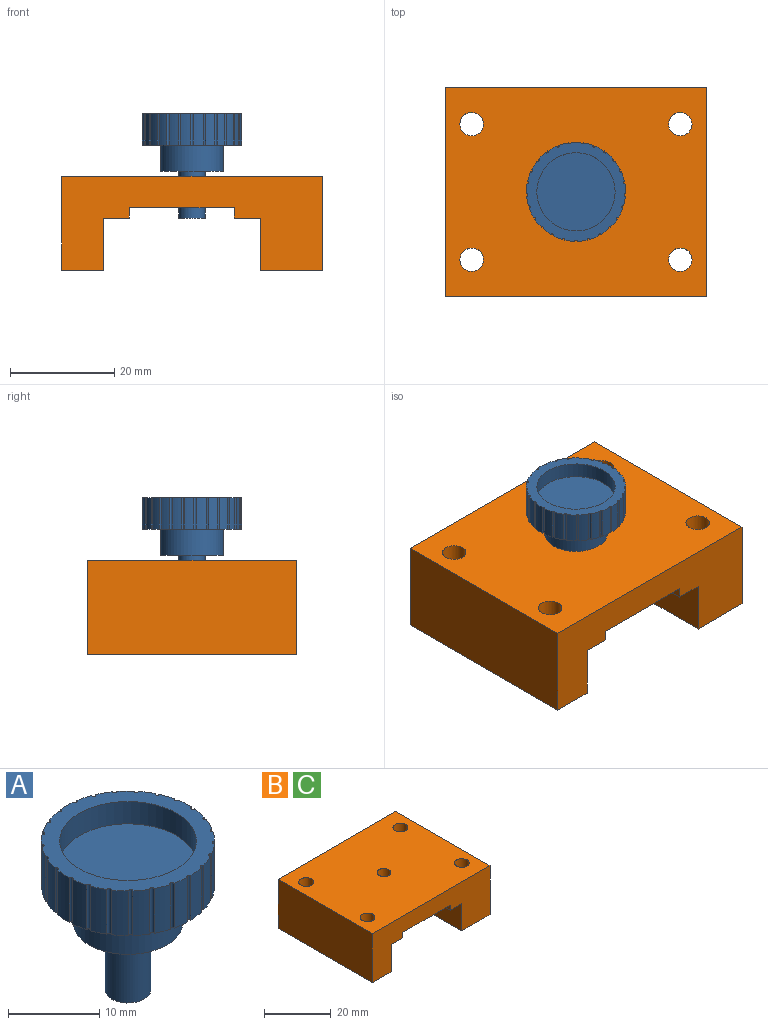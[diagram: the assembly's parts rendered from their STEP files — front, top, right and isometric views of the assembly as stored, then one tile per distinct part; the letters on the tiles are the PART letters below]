
ASSEMBLY  parts=3 mates=1
PART A: 58 faces, bbox 19x19x20 mm
  f0: plane 12x12mm, normal (0,0,-1), area 93.5mm2, adj f1,f3
  f1: cylinder r=2.5mm len=9mm, axis (0,0,1), area 141.4mm2, adj f0,f2
  f2: plane 5x5mm, normal (0,0,-1), area 19.6mm2, adj f1
  f3: cylinder r=6mm len=12mm, axis (0,0,-1), area 188.5mm2, adj f0,f4
  f4: plane 19x19mm, normal (0,0,-1), area 168mm2, adj f3,f6,f7,f8,f9,f10,f11,f12
  f5: plane 19x19mm, normal (0,0,1), area 104.4mm2, adj f6,f7,f8,f9,f10,f11,f12,f13
  f6: cylinder r=9.5mm len=6mm, axis (0,0,-1), area 11.3mm2, adj f4,f5,f7,f55
  f7: cylinder r=0.25mm len=6mm, axis (0,0,-1), area 4.7mm2, adj f4,f5,f6,f8
  f8: cylinder r=9.5mm len=6mm, axis (0,0,-1), area 11.3mm2, adj f4,f5,f7,f9
  f9: cylinder r=0.25mm len=6mm, axis (0,0,-1), area 4.7mm2, adj f4,f5,f8,f10
  f10: cylinder r=9.5mm len=6mm, axis (0,0,-1), area 11.3mm2, adj f4,f5,f9,f11
  f11: cylinder r=0.25mm len=6mm, axis (0,0,-1), area 4.7mm2, adj f4,f5,f10,f12
  f12: cylinder r=9.5mm len=6mm, axis (0,0,-1), area 11.3mm2, adj f4,f5,f11,f13
  f13: cylinder r=0.25mm len=6mm, axis (0,0,-1), area 4.7mm2, adj f4,f5,f12,f14
  f14: cylinder r=9.5mm len=6mm, axis (0,0,-1), area 11.3mm2, adj f4,f5,f13,f15
  f15: cylinder r=0.25mm len=6mm, axis (0,0,-1), area 4.7mm2, adj f4,f5,f14,f16
  f16: cylinder r=9.5mm len=6mm, axis (0,0,-1), area 11.3mm2, adj f4,f5,f15,f17
  f17: cylinder r=0.25mm len=6mm, axis (0,0,-1), area 4.7mm2, adj f4,f5,f16,f18
  f18: cylinder r=9.5mm len=6mm, axis (0,0,-1), area 11.3mm2, adj f4,f5,f17,f19
  f19: cylinder r=0.25mm len=6mm, axis (0,0,-1), area 4.7mm2, adj f4,f5,f18,f20
  f20: cylinder r=9.5mm len=6mm, axis (0,0,-1), area 11.3mm2, adj f4,f5,f19,f21
  f21: cylinder r=0.25mm len=6mm, axis (0,0,-1), area 4.7mm2, adj f4,f5,f20,f22
  f22: cylinder r=9.5mm len=6mm, axis (0,0,-1), area 11.3mm2, adj f4,f5,f21,f23
  f23: cylinder r=0.25mm len=6mm, axis (0,0,-1), area 4.7mm2, adj f4,f5,f22,f24
  f24: cylinder r=9.5mm len=6mm, axis (0,0,-1), area 11.3mm2, adj f4,f5,f23,f25
  f25: cylinder r=0.25mm len=6mm, axis (0,0,-1), area 4.7mm2, adj f4,f5,f24,f26
  f26: cylinder r=9.5mm len=6mm, axis (0,0,-1), area 11.3mm2, adj f4,f5,f25,f27
  f27: cylinder r=0.25mm len=6mm, axis (0,0,-1), area 4.7mm2, adj f4,f5,f26,f28
  f28: cylinder r=9.5mm len=6mm, axis (0,0,-1), area 11.3mm2, adj f4,f5,f27,f29
  f29: cylinder r=0.25mm len=6mm, axis (0,0,-1), area 4.7mm2, adj f4,f5,f28,f30
  f30: cylinder r=9.5mm len=6mm, axis (0,0,-1), area 11.3mm2, adj f4,f5,f29,f31
  f31: cylinder r=0.25mm len=6mm, axis (0,0,-1), area 4.7mm2, adj f4,f5,f30,f32
  f32: cylinder r=9.5mm len=6mm, axis (0,0,-1), area 11.3mm2, adj f4,f5,f31,f33
  f33: cylinder r=0.25mm len=6mm, axis (0,0,-1), area 4.7mm2, adj f4,f5,f32,f34
  f34: cylinder r=9.5mm len=6mm, axis (0,0,-1), area 11.3mm2, adj f4,f5,f33,f35
  f35: cylinder r=0.25mm len=6mm, axis (0,0,-1), area 4.7mm2, adj f4,f5,f34,f36
  f36: cylinder r=9.5mm len=6mm, axis (0,0,-1), area 11.3mm2, adj f4,f5,f35,f37
  f37: cylinder r=0.25mm len=6mm, axis (0,0,-1), area 4.7mm2, adj f4,f5,f36,f38
  f38: cylinder r=9.5mm len=6mm, axis (0,0,-1), area 11.3mm2, adj f4,f5,f37,f39
  f39: cylinder r=0.25mm len=6mm, axis (0,0,-1), area 4.7mm2, adj f4,f5,f38,f40
  f40: cylinder r=9.5mm len=6mm, axis (0,0,-1), area 11.3mm2, adj f4,f5,f39,f41
  f41: cylinder r=0.25mm len=6mm, axis (0,0,-1), area 4.7mm2, adj f4,f5,f40,f42
  f42: cylinder r=9.5mm len=6mm, axis (0,0,-1), area 11.3mm2, adj f4,f5,f41,f43
  f43: cylinder r=0.25mm len=6mm, axis (0,0,-1), area 4.7mm2, adj f4,f5,f42,f44
  f44: cylinder r=9.5mm len=6mm, axis (0,0,-1), area 11.3mm2, adj f4,f5,f43,f45
  f45: cylinder r=0.25mm len=6mm, axis (0,0,-1), area 4.7mm2, adj f4,f5,f44,f46
  f46: cylinder r=9.5mm len=6mm, axis (0,0,-1), area 11.3mm2, adj f4,f5,f45,f47
  f47: cylinder r=0.25mm len=6mm, axis (0,0,-1), area 4.7mm2, adj f4,f5,f46,f48
  f48: cylinder r=9.5mm len=6mm, axis (0,0,-1), area 11.3mm2, adj f4,f5,f47,f49
  f49: cylinder r=0.25mm len=6mm, axis (0,0,-1), area 4.7mm2, adj f4,f5,f48,f50
  f50: cylinder r=9.5mm len=6mm, axis (0,0,-1), area 11.3mm2, adj f4,f5,f49,f51
  f51: cylinder r=0.25mm len=6mm, axis (0,0,-1), area 4.7mm2, adj f4,f5,f50,f52
  f52: cylinder r=9.5mm len=6mm, axis (0,0,-1), area 11.3mm2, adj f4,f5,f51,f53
  f53: cylinder r=0.25mm len=6mm, axis (0,0,-1), area 4.7mm2, adj f4,f5,f52,f54
  f54: cylinder r=9.5mm len=6mm, axis (0,0,-1), area 11.3mm2, adj f4,f5,f53,f55
  f55: cylinder r=0.25mm len=6mm, axis (0,0,-1), area 4.7mm2, adj f4,f5,f6,f54
  f56: cylinder r=7.5mm len=15mm, axis (0,0,1), area 141.4mm2, adj f5,f57
  f57: plane 15x15mm, normal (0,0,1), area 176.7mm2, adj f56
PART B: 20 faces, bbox 50x40x18 mm
  f0: plane 40x10mm, normal (1,0,0), area 400mm2, adj f1,f11,f12,f13
  f1: plane 40x5mm, normal (0,0,-1), area 200mm2, adj f0,f2,f12,f13
  f2: plane 40x2mm, normal (1,0,0), area 80mm2, adj f1,f3,f12,f13
  f3: plane 40x20.11mm, normal (0,0,-1), area 790.5mm2, adj f2,f4,f12,f13,f14
  f4: plane 40x2mm, normal (-1,0,0), area 80mm2, adj f3,f5,f12,f13
  f5: plane 40x5mm, normal (0,0,-1), area 200mm2, adj f4,f6,f12,f13
  f6: plane 40x10mm, normal (-1,0,0), area 395.1mm2, adj f5,f7,f12,f13,f19
  f7: plane 40x11.89mm, normal (0,0,-1), area 443.8mm2, adj f6,f8,f12,f13,f16,f17
  f8: plane 40x18mm, normal (1,0,0), area 715.1mm2, adj f7,f9,f12,f13,f19
  f9: plane 50x40mm, normal (0,0,1), area 1922.5mm2, adj f8,f10,f12,f13,f14,f15,f16,f17
  f10: plane 40x18mm, normal (-1,0,0), area 720mm2, adj f9,f11,f12,f13
  f11: plane 40x8mm, normal (0,0,-1), area 288.2mm2, adj f0,f10,f12,f13,f15,f18
  f12: plane 50x18mm, normal (0,-1,0), area 558.7mm2, adj f0,f1,f2,f3,f4,f5,f6,f7
  f13: plane 50x18mm, normal (0,1,0), area 558.7mm2, adj f0,f1,f2,f3,f4,f5,f6,f7
  f14: cylinder r=2.1mm len=6mm, axis (0,0,1), area 79.2mm2, adj f3,f9
  f15: cylinder r=2.25mm len=18mm, axis (0,0,1), area 254.5mm2, adj f9,f11
  f16: cylinder r=2.25mm len=18mm, axis (0,0,1), area 254.5mm2, adj f7,f9
  f17: cylinder r=2.25mm len=18mm, axis (0,0,1), area 254.5mm2, adj f7,f9
  f18: cylinder r=2.25mm len=18mm, axis (0,0,1), area 254.5mm2, adj f9,f11
  f19: cylinder r=1.25mm len=11.89mm, axis (1,0,0), area 93.4mm2, adj f6,f8
PART C: same geometry as B
PLACE A t=(-7.71,-2.96,-4.18)mm
PLACE B t=(-1.93,-2.96,-6.52)mm
PLACE C t=(-1.93,-2.96,-6.52)mm
MATE cylindrical A.f1 <-> B.f14  axis (0,0,1) through (-7.71,-2.96,-3.43)mm
